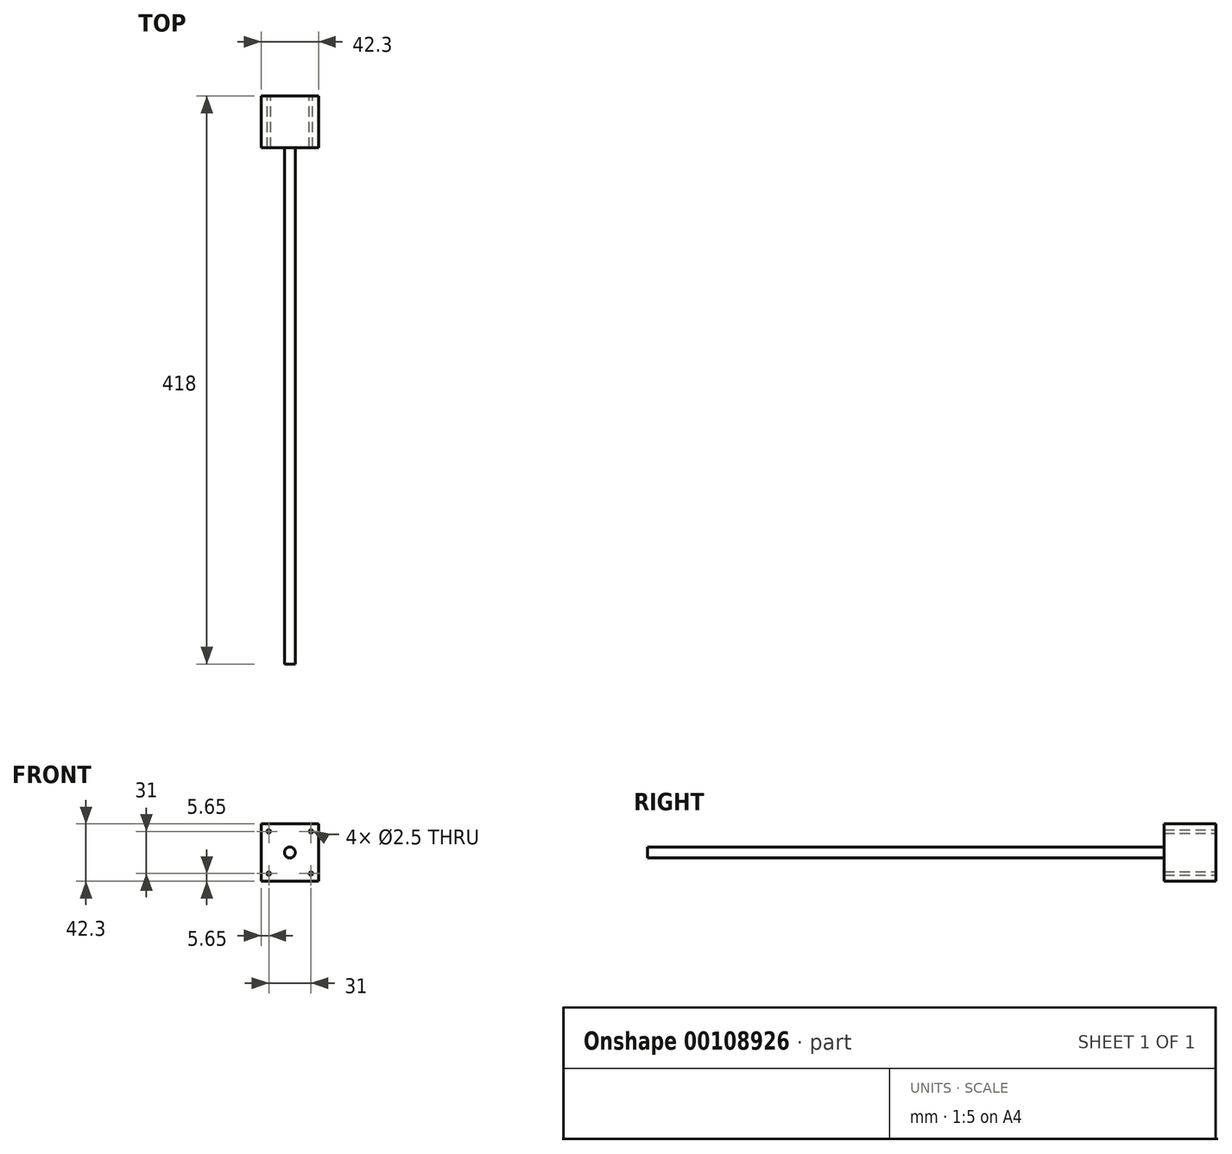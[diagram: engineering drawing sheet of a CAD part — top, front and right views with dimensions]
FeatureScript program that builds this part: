
annotation { "Feature Type Name" : "Feature", "Feature Type Description" : "" }
export const myFeature = defineFeature(function(context is Context, id is Id, definition is map)
    precondition{}
    {
        {
            var Q0;
            Q0=qCreatedBy(makeId("Front.planeOp"),FACE);
            var sketch = newSketch(context, id + "F0", { "sketchPlane" : qUnion([Q0])});
            skLineSegment(sketch, "E0.bottom", {"start": v(21.15, -21.15) * mm, "end": v(-21.15, -21.15) * mm});
            skLineSegment(sketch, "E0.top", {"start": v(21.15, 21.15) * mm, "end": v(-21.15, 21.15) * mm});
            skLineSegment(sketch, "E0.left", {"start": v(21.15, -21.15) * mm, "end": v(21.15, 21.15) * mm});
            skLineSegment(sketch, "E0.right", {"start": v(-21.15, -21.15) * mm, "end": v(-21.15, 21.15) * mm});
            skPoint(sketch, "E0.middle", {"position": v(0, 0) * mm});
            skLineSegment(sketch, "E1.bottom", {"start": v(15.5, 15.5) * mm, "end": v(-15.5, 15.5) * mm, "construction": true});
            skLineSegment(sketch, "E1.top", {"start": v(15.5, -15.5) * mm, "end": v(-15.5, -15.5) * mm, "construction": true});
            skLineSegment(sketch, "E1.left", {"start": v(15.5, 15.5) * mm, "end": v(15.5, -15.5) * mm, "construction": true});
            skLineSegment(sketch, "E1.right", {"start": v(-15.5, 15.5) * mm, "end": v(-15.5, -15.5) * mm, "construction": true});
            skPoint(sketch, "E2", {"position": v(-15.5, 15.5) * mm});
            skPoint(sketch, "E3", {"position": v(15.5, 15.5) * mm});
            skPoint(sketch, "E4", {"position": v(15.5, -15.5) * mm});
            skPoint(sketch, "E5", {"position": v(-15.5, -15.5) * mm});
            skCircle(sketch, "E6", {"center": v(-15.5, 15.5) * mm, "radius": 1.25 * mm});
            skCircle(sketch, "E7", {"center": v(15.5, 15.5) * mm, "radius": 1.25 * mm});
            skCircle(sketch, "E8", {"center": v(15.5, -15.5) * mm, "radius": 1.25 * mm});
            skCircle(sketch, "E9", {"center": v(-15.5, -15.5) * mm, "radius": 1.25 * mm});
            skSolve(sketch);
        }
        {
            var Q0;
            Q0=qSketchRegion(id+"F0",true);
            extrude(context, id + "F1", {"entities" : qUnion([Q0]), "endBound" : BoundingType.SYMMETRIC, "depth" : 38 * mm});
        }
        {
            var Q0;
            Q0=makeQuery(id+"F1.opExtrude","CAP_FACE",FACE,{"disambiguationData":[OSD([sQuery(id+"F0.wireOp",EDGE,"E0.bottom"),sQuery(id+"F0.wireOp",EDGE,"E0.top"),sQuery(id+"F0.wireOp",EDGE,"E0.left"),sQuery(id+"F0.wireOp",EDGE,"E0.right"),sQuery(id+"F0.wireOp",EDGE,"E6"),sQuery(id+"F0.wireOp",EDGE,"E7"),sQuery(id+"F0.wireOp",EDGE,"E8"),sQuery(id+"F0.wireOp",EDGE,"E9")])],"isStart":false});
            var sketch = newSketch(context, id + "F2", { "sketchPlane" : qUnion([Q0])});
            skCircle(sketch, "E10", {"center": v(0, 0) * mm, "radius": 4 * mm});
            skSolve(sketch);
        }
        {
            var Q0;
            Q0=qSketchRegion(id+"F2",true);
            extrude(context, id + "F3", {"entities" : qUnion([Q0]), "operationType" : NewBodyOperationType.ADD, "depth" : 380 * mm});
        }
    });
